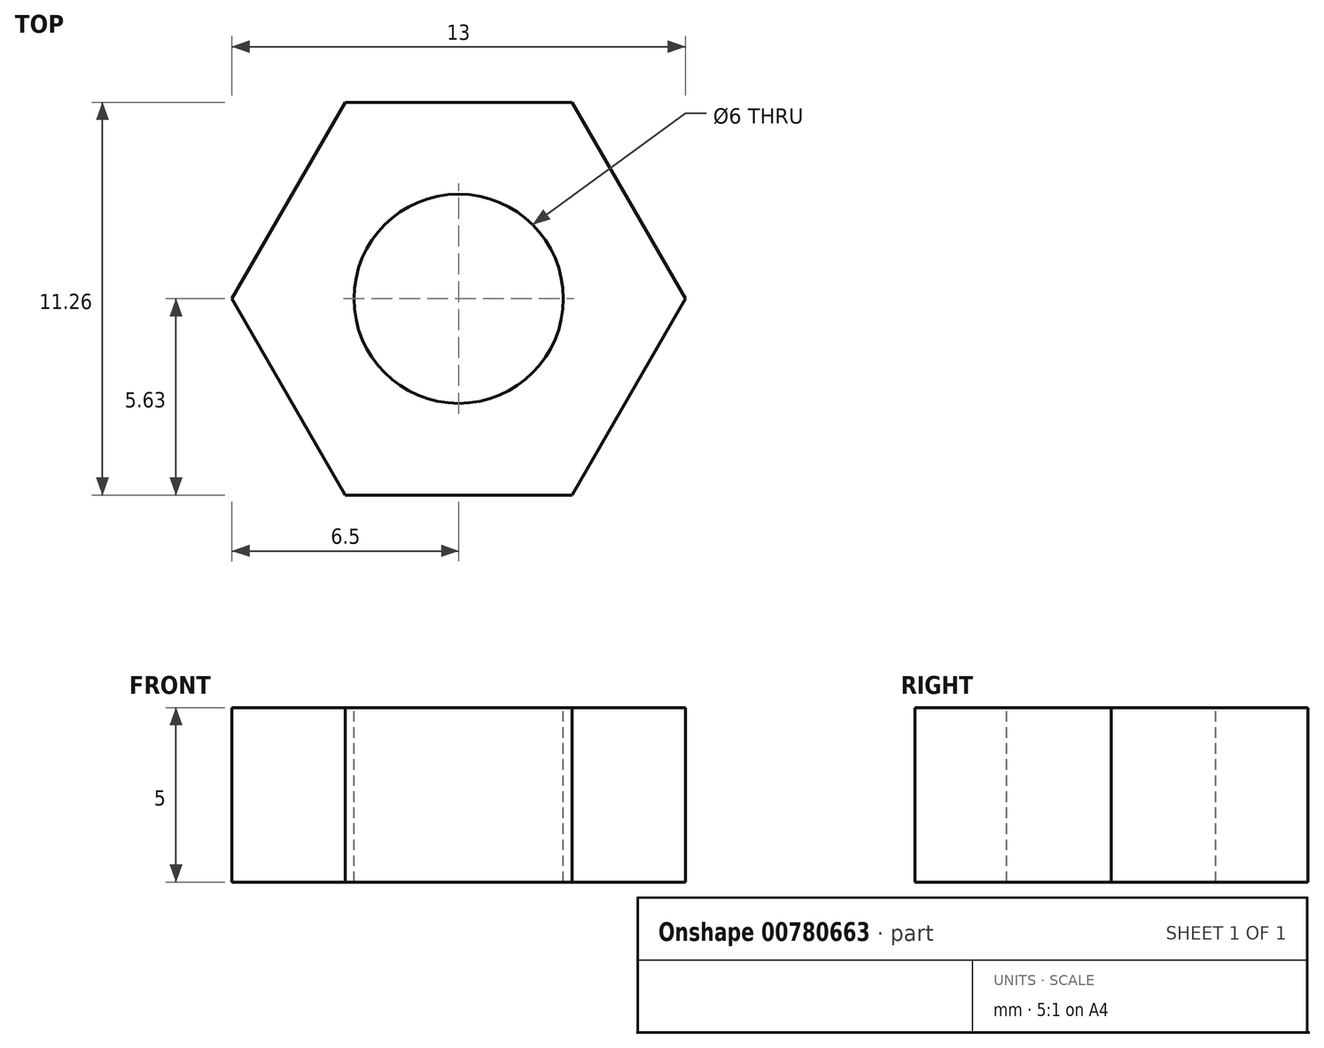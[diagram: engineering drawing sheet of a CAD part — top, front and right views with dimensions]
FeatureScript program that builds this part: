
annotation { "Feature Type Name" : "Feature", "Feature Type Description" : "" }
export const myFeature = defineFeature(function(context is Context, id is Id, definition is map)
    precondition{}
    {
        {
            var Q0;
            Q0=qCreatedBy(makeId("Top.planeOp"),FACE);
            var sketch = newSketch(context, id + "F0", { "sketchPlane" : qUnion([Q0])});
            skCircle(sketch, "E0", {"center": v(0, 0) * mm, "radius": 6.5 * mm});
            skSolve(sketch);
        }
        {
            var Q0;
            Q0 = qSketchRegion(id + "F0", true);
            extrude(context, id + "F1", {"entities" : qUnion([Q0]), "oppositeDirection" : true, "depth" : 5 * mm, "offsetDistance" : 25 * mm});
        }
        {
            var Q0;
            Q0=makeQuery(id+"F1.opExtrude","CAP_FACE",FACE,{"disambiguationData":[OSD([sQuery(id+"F0.wireOp",EDGE,"E0")])],"isStart":true});
            var sketch = newSketch(context, id + "F2", { "sketchPlane" : qUnion([Q0])});
            skCircle(sketch, "E1.cCircle", {"center": v(0, 0) * mm, "radius": 6.5 * mm, "construction": true});
            skLineSegment(sketch, "E1.0", {"start": v(6.5, 0) * mm, "end": v(3.25, -5.63) * mm});
            skLineSegment(sketch, "E1.1", {"start": v(3.25, -5.63) * mm, "end": v(-3.25, -5.63) * mm});
            skLineSegment(sketch, "E1.2", {"start": v(-3.25, -5.63) * mm, "end": v(-6.5, 0) * mm});
            skLineSegment(sketch, "E1.3", {"start": v(-6.5, 0) * mm, "end": v(-3.25, 5.63) * mm});
            skLineSegment(sketch, "E1.4", {"start": v(-3.25, 5.63) * mm, "end": v(3.25, 5.63) * mm});
            skLineSegment(sketch, "E1.5", {"start": v(3.25, 5.63) * mm, "end": v(6.5, 0) * mm});
            skSolve(sketch);
        }
        {
            var Q0;
            {var subQ0=sQuery(id+"F2.wireOp",EDGE,"E1.4");Q0=makeQuery(id+"F2.imprint","IMPRINT",FACE,{"disambiguationData":[TD([[makeQuery(id+"F2.imprint","IMPRINT",EDGE,{"derivedFrom":subQ0}),1.0]])]});}
            var Q1;
            {var subQ0=sQuery(id+"F2.wireOp",EDGE,"E1.3");Q1=makeQuery(id+"F2.imprint","IMPRINT",FACE,{"disambiguationData":[TD([[makeQuery(id+"F2.imprint","IMPRINT",EDGE,{"derivedFrom":subQ0}),1.0]])]});}
            var Q2;
            {var subQ0=sQuery(id+"F2.wireOp",EDGE,"E1.2");Q2=makeQuery(id+"F2.imprint","IMPRINT",FACE,{"disambiguationData":[TD([[makeQuery(id+"F2.imprint","IMPRINT",EDGE,{"derivedFrom":subQ0}),1.0]])]});}
            var Q3;
            {var subQ0=sQuery(id+"F2.wireOp",EDGE,"E1.1");Q3=makeQuery(id+"F2.imprint","IMPRINT",FACE,{"disambiguationData":[TD([[makeQuery(id+"F2.imprint","IMPRINT",EDGE,{"derivedFrom":subQ0}),1.0]])]});}
            var Q4;
            {var subQ0=sQuery(id+"F2.wireOp",EDGE,"E1.0");Q4=makeQuery(id+"F2.imprint","IMPRINT",FACE,{"disambiguationData":[TD([[makeQuery(id+"F2.imprint","IMPRINT",EDGE,{"derivedFrom":subQ0}),1.0]])]});}
            var Q5;
            {var subQ0=sQuery(id+"F2.wireOp",EDGE,"E1.5");Q5=makeQuery(id+"F2.imprint","IMPRINT",FACE,{"disambiguationData":[TD([[makeQuery(id+"F2.imprint","IMPRINT",EDGE,{"derivedFrom":subQ0}),1.0]])]});}
            extrude(context, id + "F3", {"entities" : qUnion([Q0, Q1, Q2, Q3, Q4, Q5]), "operationType" : NewBodyOperationType.REMOVE, "endBound" : BoundingType.THROUGH_ALL, "oppositeDirection" : true, "depth" : 25 * mm, "offsetDistance" : 25 * mm});
        }
        {
            var Q0;
            Q0=makeQuery(id+"F1.opExtrude","CAP_FACE",FACE,{"disambiguationData":[OSD([sQuery(id+"F0.wireOp",EDGE,"E0")])],"isStart":true});
            var sketch = newSketch(context, id + "F4", { "sketchPlane" : qUnion([Q0])});
            skCircle(sketch, "E2", {"center": v(0, 0) * mm, "radius": 3 * mm});
            skSolve(sketch);
        }
        {
            var Q0;
            Q0 = qSketchRegion(id + "F4", true);
            extrude(context, id + "F5", {"entities" : qUnion([Q0]), "operationType" : NewBodyOperationType.REMOVE, "endBound" : BoundingType.THROUGH_ALL, "oppositeDirection" : true, "depth" : 25 * mm, "offsetDistance" : 25 * mm});
        }
    });
